# Revit family: ed
name_source: partatom
category: Generic Models
revit_build: Autodesk Revit 2018 (Build: 20190510_1515(x64)
units: mm (PartAtom-declared; Revit-internal decimal feet)

## family parameters
Can host rebar = No
Cut with Voids When Loaded = No
Host = Face
OmniClass Number = 23.31.17.00
OmniClass Title = Showers
Part Type = Normal
Room Calculation Point = No
Round Connector Dimension = Use Diameter
Shared = No

## types (1)
- Hand shower holder 52x34x34 mm - UV0620000
    BIMobject category = Showers
    Default Elevation = 1219 mm
    Description = Duravit Hand shower holder Chrome High Gloss 52x34x34 mm - UV0620000000
    Design country = Germany
    ETIM classification = EC010132 | Hand shower holder
    Edition number = 1
    IFC Classification = Sanitary Terminal
    Installation instructions = https://pro.duravit.com
    Main material = Duravit - Metal - 10 - Chrome
    Manufacturer = Duravit
    Manufacturer country = Germany
    Manufacturer name = DURAVIT AG
    Masterformat 2014 Code = 22 41 23
    Masterformat 2014 Description = Residential Showers
    Material main = Brass
    Model = Hand shower holder 52x34x34 mm - UV0620000
    OmniClass Code = 23-31 17 00
    OmniClass Description = Showers
    Product Guid = fda71cd4-8b78-429d-9606-ddf5c0ccadbe
    Product SKU = Hand-shower-holder-52x34x34-mm-UV0620000
    Product certification = https://pro.duravit.com
    Product data url = https://bimobject.com
    Product family = Universal
    Product group = Hand shower holder
    Product name = Hand shower holder 52x34x34 mm - UV0620000
    Product url = https://pro.duravit.com
    QR code = https://bimobject.com
    Technical description = https://pro.duravit.com
    UNSPSC Code = 30181503
    URL = https://www.duravit.com
    Uniclass 2015 Code = SL_35_80_80
    Uniclass 2015 Name = Showers
    Uniformat II Code = D2010
    Uniformat II Description = Plumbing Fixtures
    Weight Net (Kg) = 0.027
    Youtube clip = https://pro.duravit.com

## geometry (parser evidence)
native form markers: Sweep x4
no freeform markers — native parametric forms only
